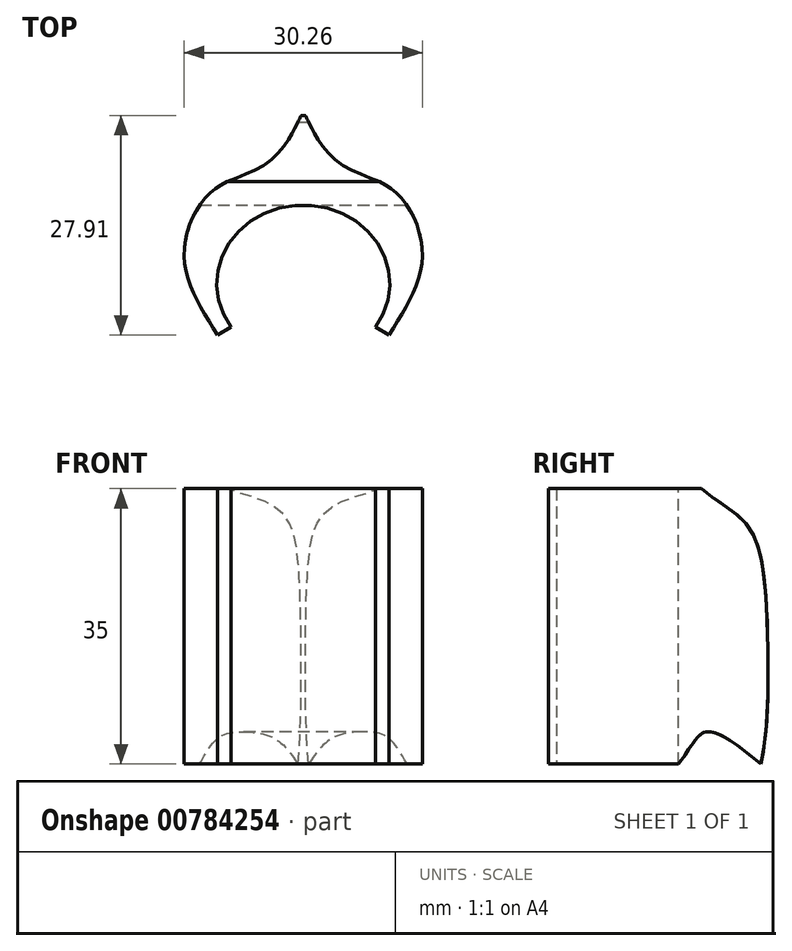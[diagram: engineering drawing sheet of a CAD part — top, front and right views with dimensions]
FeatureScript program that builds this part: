
annotation { "Feature Type Name" : "Feature", "Feature Type Description" : "" }
export const myFeature = defineFeature(function(context is Context, id is Id, definition is map)
    precondition{}
    {
        {
            var Q0;
            Q0=qCreatedBy(makeId("Top.planeOp"),FACE);
            var sketch = newSketch(context, id + "F0", { "sketchPlane" : qUnion([Q0])});
            skEllipticalArc(sketch, "E0", {});
            skFitSpline(sketch, "E1", {"points": [v(-10.9, -6.53) * mm, v(-15.1, 2.92) * mm, v(-11.63, 11.72) * mm, v(-5.02, 15.01) * mm, v(0, 22) * mm], "startDerivative": vector(-20.46, 34.97) * mm, "endDerivative": vector(15.4, 36.28) * mm});
            skLineSegment(sketch, "E2", {"start": v(0, 0) * mm, "end": v(0, 22) * mm, "construction": true});
            skFitSpline(sketch, "E3.MirrorCS", {"points": [v(10.9, -6.53) * mm, v(15.1, 2.92) * mm, v(11.63, 11.72) * mm, v(5.02, 15.01) * mm, v(0, 22) * mm], "startDerivative": vector(20.46, 34.97) * mm, "endDerivative": vector(-15.4, 36.28) * mm});
            skLineSegment(sketch, "E4", {"start": v(-10.9, -6.53) * mm, "end": v(-9.19, -5.5) * mm});
            skLineSegment(sketch, "E5.MirrorCS", {"start": v(10.9, -6.53) * mm, "end": v(9.19, -5.5) * mm});
            const initialGuessF0  = {"E0": [0, 0, -1, 0, 0.011, 0.01, 2.5592284157210505, 0.5823642378687437]};
            skSetInitialGuess(sketch, initialGuessF0);
            skSolve(sketch);
        }
        {
            var Q0;
            Q0=makeQuery(id+"F0.imprint","IMPRINT",FACE,{"disambiguationData":[TD([[makeQuery(id+"F0.imprint","IMPRINT",EDGE,{"derivedFrom":sQuery(id+"F0.wireOp",EDGE,"E0")}),-1.0]])]});
            extrude(context, id + "F1", {"entities" : qUnion([Q0]), "endBound" : BoundingType.SYMMETRIC, "depth" : 35 * mm, "offsetDistance" : 25 * mm});
        }
        {
            var Q0;
            Q0=qCreatedBy(makeId("Right.planeOp"),FACE);
            var sketch = newSketch(context, id + "F2", { "sketchPlane" : qUnion([Q0])});
            skLineSegment(sketch, "E6.0", {"start": v(22, 17.5) * mm, "end": v(22, -17.5) * mm});
            skLineSegment(sketch, "E7", {"start": v(10, 17.5) * mm, "end": v(10, -17.5) * mm});
            skLineSegment(sketch, "E8.0.0", {"start": v(-6.53, -17.5) * mm, "end": v(-5.5, -17.5) * mm});
            skLineSegment(sketch, "E8.0.1", {"start": v(-5.5, -17.5) * mm, "end": v(10, -17.5) * mm});
            skLineSegment(sketch, "E8.0.2", {"start": v(-5.5, -17.5) * mm, "end": v(-6.53, -17.5) * mm});
            skFitSpline(sketch, "E8.0.3", {"points": [v(-6.53, -17.5) * mm, v(-3.39, -17.5) * mm, v(2.32, -17.5) * mm, v(13.06, -17.5) * mm, v(14.02, -17.5) * mm, v(19.03, -17.5) * mm, v(22, -17.5) * mm]});
            skFitSpline(sketch, "E8.0.4", {"points": [v(22, -17.5) * mm, v(19.03, -17.5) * mm, v(14.02, -17.5) * mm, v(13.06, -17.5) * mm, v(2.32, -17.5) * mm, v(-3.39, -17.5) * mm, v(-6.53, -17.5) * mm]});
            skFitSpline(sketch, "E9", {"points": [v(20.49, -17.5) * mm, v(21.37, -4.57) * mm, v(20.15, 9.95) * mm, v(17, 14.53) * mm, v(11.58, 19.21) * mm], "startDerivative": vector(8.49, 40.76) * mm, "endDerivative": vector(-15.77, 29.22) * mm});
            skLineSegment(sketch, "E10.0.0", {"start": v(-5.5, 17.5) * mm, "end": v(-6.53, 17.5) * mm});
            skFitSpline(sketch, "E10.0.1", {"points": [v(-6.53, 17.5) * mm, v(-3.39, 17.5) * mm, v(2.32, 17.5) * mm, v(13.06, 17.5) * mm, v(14.02, 17.5) * mm, v(19.03, 17.5) * mm, v(22, 17.5) * mm]});
            skFitSpline(sketch, "E10.0.2", {"points": [v(22, 17.5) * mm, v(19.03, 17.5) * mm, v(14.02, 17.5) * mm, v(13.06, 17.5) * mm, v(2.32, 17.5) * mm, v(-3.39, 17.5) * mm, v(-6.53, 17.5) * mm]});
            skLineSegment(sketch, "E10.0.3", {"start": v(-6.53, 17.5) * mm, "end": v(-5.5, 17.5) * mm});
            skLineSegment(sketch, "E10.0.4", {"start": v(-5.5, 17.5) * mm, "end": v(10, 17.5) * mm});
            skLineSegment(sketch, "E11", {"start": v(22, 17.5) * mm, "end": v(12.95, 17.5) * mm});
            skLineSegment(sketch, "E12", {"start": v(22, -17.5) * mm, "end": v(20.49, -17.5) * mm});
            skSolve(sketch);
        }
        {
            var Q0;
            Q0=makeQuery(id+"F2.imprint","IMPRINT",FACE,{"disambiguationData":[TD([[makeQuery(id+"F2.imprint","IMPRINT",EDGE,{"derivedFrom":sQuery(id+"F2.wireOp",EDGE,"E6.0")}),-1.0]])]});
            extrude(context, id + "F3", {"entities" : qUnion([Q0]), "operationType" : NewBodyOperationType.REMOVE, "endBound" : BoundingType.THROUGH_ALL, "depth" : 25 * mm, "offsetDistance" : 25 * mm, "hasSecondDirection" : true, "secondDirectionBound" : SecondDirectionBoundingType.THROUGH_ALL, "secondDirectionOppositeDirection" : true, "secondDirectionDepth" : 25 * mm});
        }
        {
            var Q0;
            Q0=qCreatedBy(makeId("Right.planeOp"),FACE);
            var sketch = newSketch(context, id + "F4", { "sketchPlane" : qUnion([Q0])});
            skFitSpline(sketch, "E13.0.1", {"points": [v(22, -17.5) * mm, v(19.03, -17.5) * mm, v(14.02, -17.5) * mm, v(13.06, -17.5) * mm, v(2.32, -17.5) * mm, v(-3.39, -17.5) * mm, v(-6.53, -17.5) * mm]});
            skLineSegment(sketch, "E13.0.2", {"start": v(-6.53, -17.5) * mm, "end": v(-5.5, -17.5) * mm});
            skLineSegment(sketch, "E13.0.3", {"start": v(-5.5, -17.5) * mm, "end": v(10, -17.5) * mm});
            skLineSegment(sketch, "E13.0.4", {"start": v(-5.5, -17.5) * mm, "end": v(-6.53, -17.5) * mm});
            skFitSpline(sketch, "E13.0.5", {"points": [v(-6.53, -17.5) * mm, v(-3.39, -17.5) * mm, v(2.32, -17.5) * mm, v(13.06, -17.5) * mm, v(14.02, -17.5) * mm, v(19.03, -17.5) * mm, v(22, -17.5) * mm]});
            skFitSpline(sketch, "E14.0.0", {"points": [v(-6.53, 17.5) * mm, v(-3.39, 17.5) * mm, v(2.32, 17.5) * mm, v(13.06, 17.5) * mm, v(14.02, 17.5) * mm, v(19.03, 17.5) * mm, v(22, 17.5) * mm]});
            skFitSpline(sketch, "E14.0.2", {"points": [v(22, 17.5) * mm, v(19.03, 17.5) * mm, v(14.02, 17.5) * mm, v(13.06, 17.5) * mm, v(2.32, 17.5) * mm, v(-3.39, 17.5) * mm, v(-6.53, 17.5) * mm]});
            skLineSegment(sketch, "E14.0.3", {"start": v(-6.53, 17.5) * mm, "end": v(-5.5, 17.5) * mm});
            skLineSegment(sketch, "E14.0.4", {"start": v(-5.5, 17.5) * mm, "end": v(10, 17.5) * mm});
            skLineSegment(sketch, "E14.0.5", {"start": v(-5.5, 17.5) * mm, "end": v(-6.53, 17.5) * mm});
            skFitSpline(sketch, "E15.0.1", {"points": [v(20.49, -17.5) * mm, v(20.85, -15.77) * mm, v(21.17, -13.15) * mm, v(21.34, -9.64) * mm, v(21.38, -7) * mm, v(21.38, -4.35) * mm, v(21.35, -1.7) * mm, v(21.27, 0.94) * mm, v(21.13, 3.58) * mm, v(20.9, 6.21) * mm, v(20.56, 8.38) * mm, v(20.13, 10.1) * mm, v(19.77, 11.1) * mm, v(19.39, 11.88) * mm, v(18.95, 12.62) * mm, v(18.3, 13.42) * mm, v(17.43, 14.23) * mm, v(16.7, 14.77) * mm, v(16.12, 15.16) * mm, v(15.57, 15.53) * mm, v(14.71, 16.11) * mm, v(14.04, 16.59) * mm, v(13.44, 17.06) * mm, v(13.12, 17.34) * mm, v(12.95, 17.5) * mm]});
            skFitSpline(sketch, "E15.0.3", {"points": [v(12.95, 17.5) * mm, v(13.12, 17.34) * mm, v(13.44, 17.06) * mm, v(14.04, 16.59) * mm, v(14.71, 16.11) * mm, v(15.57, 15.53) * mm, v(16.12, 15.16) * mm, v(16.7, 14.77) * mm, v(17.43, 14.23) * mm, v(18.3, 13.42) * mm, v(18.95, 12.62) * mm, v(19.39, 11.88) * mm, v(19.77, 11.1) * mm, v(20.13, 10.1) * mm, v(20.56, 8.38) * mm, v(20.9, 6.21) * mm, v(21.13, 3.58) * mm, v(21.27, 0.94) * mm, v(21.35, -1.7) * mm, v(21.38, -4.35) * mm, v(21.38, -7) * mm, v(21.34, -9.64) * mm, v(21.17, -13.15) * mm, v(20.85, -15.77) * mm, v(20.49, -17.5) * mm]});
            skLineSegment(sketch, "E16", {"start": v(10, 17.5) * mm, "end": v(10, -17.5) * mm});
            skFitSpline(sketch, "E17", {"points": [v(20.49, -17.5) * mm, v(15.74, -14.03) * mm, v(13.74, -13.4) * mm, v(12.65, -13.86) * mm, v(10.89, -16.26) * mm, v(10, -17.5) * mm], "startDerivative": vector(-16.69, 13.47) * mm, "endDerivative": vector(-5.1, -6.74) * mm});
            skSolve(sketch);
        }
        {
            var Q0;
            {var subQ0=sQuery(id+"F4.wireOp",EDGE,"E17");Q0=makeQuery(id+"F4.imprint","IMPRINT",FACE,{"disambiguationData":[TD([[makeQuery(id+"F4.imprint","IMPRINT",EDGE,{"derivedFrom":subQ0}),1.0]])]});}
            extrude(context, id + "F5", {"entities" : qUnion([Q0]), "operationType" : NewBodyOperationType.REMOVE, "endBound" : BoundingType.THROUGH_ALL, "oppositeDirection" : true, "depth" : 25 * mm, "offsetDistance" : 25 * mm, "hasSecondDirection" : true, "secondDirectionBound" : SecondDirectionBoundingType.THROUGH_ALL, "secondDirectionOppositeDirection" : false, "secondDirectionDepth" : 25 * mm});
        }
    });
